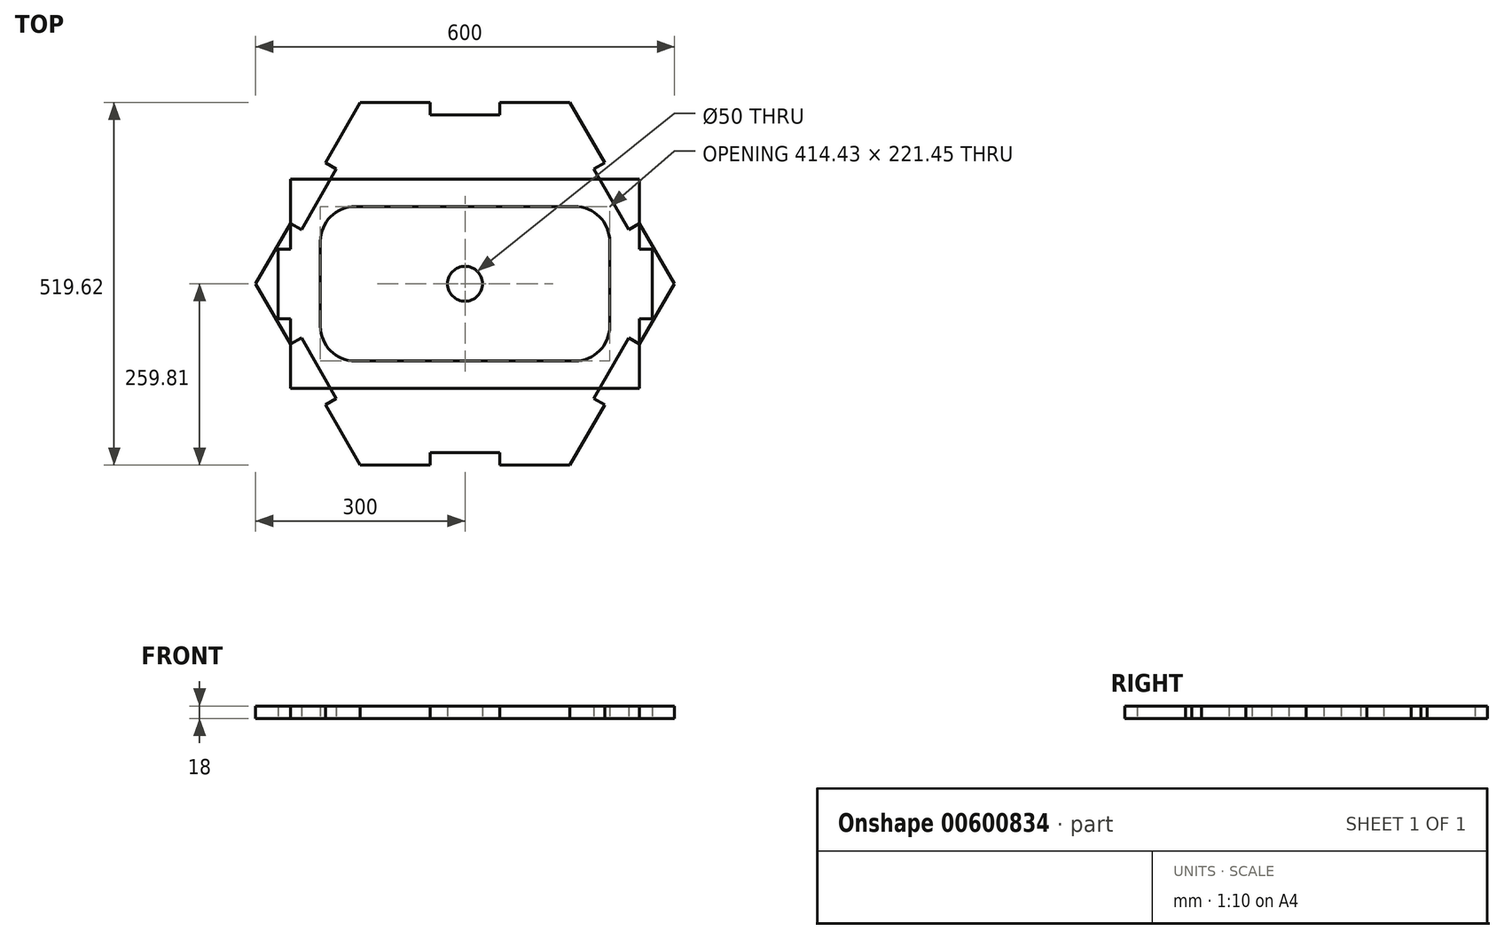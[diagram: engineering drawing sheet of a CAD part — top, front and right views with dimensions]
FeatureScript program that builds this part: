
annotation { "Feature Type Name" : "Feature", "Feature Type Description" : "" }
export const myFeature = defineFeature(function(context is Context, id is Id, definition is map)
    precondition{}
    {
        {
            var Q0;
            Q0=qCreatedBy(makeId("Top.planeOp"),FACE);
            var sketch = newSketch(context, id + "F0", { "sketchPlane" : qUnion([Q0])});
            skLineSegment(sketch, "E0", {"start": v(0, 0) * mm, "end": v(0, 369.43) * mm, "construction": true});
            skLineSegment(sketch, "E1", {"start": v(0, 369.43) * mm, "end": v(0, -332.17) * mm, "construction": true});
            skArc(sketch, "E2.cCircle", {"start": v(0, 259.8) * mm, "mid": v(-25.12, -258.6) * mm, "end": v(50, 254.95) * mm, "construction": true});
            skLineSegment(sketch, "E2.0", {"start": v(150, -259.8) * mm, "end": v(50, -259.8) * mm});
            skLineSegment(sketch, "E2.1", {"start": v(-150, -259.8) * mm, "end": v(-200, -173.2) * mm});
            skLineSegment(sketch, "E2.2", {"start": v(-300, 0) * mm, "end": v(-250, 86.6) * mm});
            skLineSegment(sketch, "E2.3", {"start": v(-150, 259.8) * mm, "end": v(-50, 259.8) * mm});
            skLineSegment(sketch, "E2.4", {"start": v(150, 259.8) * mm, "end": v(200, 173.2) * mm});
            skLineSegment(sketch, "E2.5", {"start": v(300, 0) * mm, "end": v(250, -86.6) * mm});
            skPoint(sketch, "E2.0.midPoint", {"position": v(0, -259.8) * mm});
            skLineSegment(sketch, "E3.bottom", {"start": v(50, 241.8) * mm, "end": v(-50, 241.8) * mm});
            skLineSegment(sketch, "E3.left", {"start": v(50, 241.8) * mm, "end": v(50, 259.8) * mm});
            skLineSegment(sketch, "E3.right", {"start": v(-50, 241.8) * mm, "end": v(-50, 259.8) * mm});
            skPoint(sketch, "E3.middle", {"position": v(0, 259.8) * mm});
            skLineSegment(sketch, "E4.1.0", {"start": v(-184.41, 164.2) * mm, "end": v(-200, 173.2) * mm});
            skLineSegment(sketch, "E4.1.1", {"start": v(-184.41, 164.2) * mm, "end": v(-234.41, 77.6) * mm});
            skLineSegment(sketch, "E4.1.2", {"start": v(-234.41, 77.6) * mm, "end": v(-250, 86.6) * mm});
            skLineSegment(sketch, "E4.2.0", {"start": v(-234.41, -77.6) * mm, "end": v(-250, -86.6) * mm});
            skLineSegment(sketch, "E4.2.1", {"start": v(-234.41, -77.6) * mm, "end": v(-184.41, -164.2) * mm});
            skLineSegment(sketch, "E4.2.2", {"start": v(-184.41, -164.2) * mm, "end": v(-200, -173.2) * mm});
            skLineSegment(sketch, "E4.3.0", {"start": v(-50, -241.8) * mm, "end": v(-50, -259.8) * mm});
            skLineSegment(sketch, "E4.3.1", {"start": v(-50, -241.8) * mm, "end": v(50, -241.8) * mm});
            skLineSegment(sketch, "E4.3.2", {"start": v(50, -241.8) * mm, "end": v(50, -259.8) * mm});
            skLineSegment(sketch, "E4.4.0", {"start": v(184.41, -164.2) * mm, "end": v(200, -173.2) * mm});
            skLineSegment(sketch, "E4.4.1", {"start": v(184.41, -164.2) * mm, "end": v(234.41, -77.6) * mm});
            skLineSegment(sketch, "E4.4.2", {"start": v(234.41, -77.6) * mm, "end": v(250, -86.6) * mm});
            skLineSegment(sketch, "E4.5.0", {"start": v(234.41, 77.6) * mm, "end": v(250, 86.6) * mm});
            skLineSegment(sketch, "E4.5.1", {"start": v(234.41, 77.6) * mm, "end": v(184.41, 164.2) * mm});
            skLineSegment(sketch, "E4.5.2", {"start": v(184.41, 164.2) * mm, "end": v(200, 173.2) * mm});
            skLineSegment(sketch, "E5.trimOffspring", {"start": v(0, 259.8) * mm, "end": v(150, 259.8) * mm});
            skPoint(sketch, "E6.orphan", {"position": v(215.59, 182.2) * mm});
            skPoint(sketch, "E7.orphan", {"position": v(265.59, 95.6) * mm});
            skPoint(sketch, "E8.orphan", {"position": v(265.59, -95.6) * mm});
            skPoint(sketch, "E9.orphan", {"position": v(215.59, -182.2) * mm});
            skPoint(sketch, "E10.orphan", {"position": v(50, -277.8) * mm});
            skPoint(sketch, "E11.orphan", {"position": v(-50, -277.8) * mm});
            skPoint(sketch, "E12.orphan", {"position": v(-215.59, -182.2) * mm});
            skPoint(sketch, "E13.orphan", {"position": v(-265.59, -95.6) * mm});
            skPoint(sketch, "E14.orphan", {"position": v(-265.59, 95.6) * mm});
            skPoint(sketch, "E15.orphan", {"position": v(-215.59, 182.2) * mm});
            skPoint(sketch, "E16.orphan", {"position": v(50, 277.8) * mm});
            skPoint(sketch, "E3.top.end.orphan", {"position": v(-50, 277.8) * mm});
            skLineSegment(sketch, "E17.trimOffspring", {"start": v(250, 86.6) * mm, "end": v(300, 0) * mm});
            skLineSegment(sketch, "E18.trimOffspring", {"start": v(200, -173.2) * mm, "end": v(150, -259.8) * mm});
            skLineSegment(sketch, "E19.trimOffspring", {"start": v(-50, -259.8) * mm, "end": v(-150, -259.8) * mm});
            skLineSegment(sketch, "E20.trimOffspring", {"start": v(-225, -129.9) * mm, "end": v(-300, 0) * mm});
            skLineSegment(sketch, "E21.trimOffspring", {"start": v(-200, 173.2) * mm, "end": v(-150, 259.8) * mm});
            skCircle(sketch, "E22", {"center": v(0, 0) * mm, "radius": 25 * mm});
            skSolve(sketch);
        }
        {
            var Q0;
            Q0=qCreatedBy(makeId("Top.planeOp"),FACE);
            var sketch = newSketch(context, id + "F1", { "sketchPlane" : qUnion([Q0])});
            skLineSegment(sketch, "E23.bottom", {"start": v(250, -150) * mm, "end": v(-250, -150) * mm});
            skLineSegment(sketch, "E23.top", {"start": v(250, 150) * mm, "end": v(-250, 150) * mm});
            skLineSegment(sketch, "E23.left", {"start": v(250, -150) * mm, "end": v(250, -49.88) * mm});
            skLineSegment(sketch, "E23.right", {"start": v(-250, -150) * mm, "end": v(-250, -49.88) * mm});
            skPoint(sketch, "E23.middle", {"position": v(0, 0) * mm});
            skLineSegment(sketch, "E24.top", {"start": v(268, 49.88) * mm, "end": v(250, 49.88) * mm});
            skLineSegment(sketch, "E24.left", {"start": v(268, -49.88) * mm, "end": v(268, 49.88) * mm});
            skLineSegment(sketch, "E24.right", {"start": v(-268, -49.88) * mm, "end": v(-268, 49.88) * mm});
            skLineSegment(sketch, "E25.trimOffspring", {"start": v(-250, 49.88) * mm, "end": v(-250, 150) * mm});
            skLineSegment(sketch, "E26.trimOffspring", {"start": v(250, 49.88) * mm, "end": v(250, 150) * mm});
            skLineSegment(sketch, "E27.trimOffspring", {"start": v(-250, 49.88) * mm, "end": v(-268, 49.88) * mm});
            skLineSegment(sketch, "E28.trimOffspring", {"start": v(-250, -49.88) * mm, "end": v(-268, -49.88) * mm});
            skLineSegment(sketch, "E29", {"start": v(268, -49.88) * mm, "end": v(250, -49.88) * mm});
            skLineSegment(sketch, "E30.bottom", {"start": v(157.22, -110.73) * mm, "end": v(-157.22, -110.73) * mm});
            skLineSegment(sketch, "E30.top", {"start": v(157.22, 110.73) * mm, "end": v(-157.22, 110.73) * mm});
            skLineSegment(sketch, "E30.left", {"start": v(207.22, -60.73) * mm, "end": v(207.22, 60.73) * mm});
            skLineSegment(sketch, "E30.right", {"start": v(-207.22, -60.73) * mm, "end": v(-207.22, 60.73) * mm});
            skPoint(sketch, "E31.visualSharp", {"position": v(-207.22, 110.73) * mm});
            skArc(sketch, "E31.filletArc", {"start": v(-157.22, 110.73) * mm, "mid": v(-192.57, 96.08) * mm, "end": v(-207.22, 60.73) * mm});
            skPoint(sketch, "E32.visualSharp", {"position": v(-207.22, -110.73) * mm});
            skArc(sketch, "E32.filletArc", {"start": v(-207.22, -60.73) * mm, "mid": v(-192.57, -96.08) * mm, "end": v(-157.22, -110.73) * mm});
            skPoint(sketch, "E33.visualSharp", {"position": v(207.22, -110.73) * mm});
            skArc(sketch, "E33.filletArc", {"start": v(157.22, -110.73) * mm, "mid": v(192.57, -96.08) * mm, "end": v(207.22, -60.73) * mm});
            skPoint(sketch, "E34.visualSharp", {"position": v(207.22, 110.73) * mm});
            skArc(sketch, "E34.filletArc", {"start": v(207.22, 60.73) * mm, "mid": v(192.57, 96.08) * mm, "end": v(157.22, 110.73) * mm});
            skSolve(sketch);
        }
        {
            var Q0;
            Q0=makeQuery(id+"F1.imprint","IMPRINT",FACE,{"disambiguationData":[TD([[makeQuery(id+"F1.imprint","IMPRINT",EDGE,{"derivedFrom":sQuery(id+"F1.wireOp",EDGE,"E23.bottom")}),-1.0]])]});
            extrude(context, id + "F2", {"entities" : qUnion([Q0]), "depth" : 18 * mm, "offsetDistance" : 25 * mm});
        }
        {
            var Q0;
            Q0 = qSketchRegion(id + "F0", true);
            extrude(context, id + "F3", {"entities" : qUnion([Q0]), "depth" : 18 * mm, "offsetDistance" : 25 * mm});
        }
    });
